# Revit family: Lighting_Wall-Mounted_Nordlux_MIB-6
name_source: partatom
category: Lighting Fixtures
revit_build: Autodesk Revit 2017 (Build: 20160225_1515(x64)
units: mm (PartAtom-declared; Revit-internal decimal feet)

## family parameters
Cut with Voids When Loaded = No
Host = Face
Light Source = Yes
OmniClass Number = 23.80.70.00
OmniClass Title = Lighting
Part Type = Normal
Room Calculation Point = No
Round Connector Dimension = Use Diameter
Shared = No

## types (2) — shared parameters
AssetType = Fixed
BIMObjectName = Lighting_Wall-Mounted_Nordlux_MIB-6
Category = Indoor lighting
Collection = MIB 6
Color Filter = 16777215
ConvergoRefNr = 0143-1909-0017-DK
Description = The MIB collection is based on classical virtues of design, with an emphasis on simplicity. The adjustable lamp head provides a sleek and Nordic design look. MIB is available in several variations, and as a collection offers a great variety of applications. An indestructible lighting collection that spreads light and joy in any modern home. Design by Bønnelycke MDD. The minimalist MIB series is steeped in Nordic elegance and boasts excellent usability. MIB 6 invites you to put the spotlight on life. The narrow lamp head emits a precise and narrow directional light.
Designer = Bonnelycke MDD
Dimming Lamp Color Temperature Shift = <None>
DurationUnit = Hours
Emit Shape Visible in Rendering = No
Emit from Circle Diameter = 50 mm  [stored 0.164042 ft]
EnergyClass = A++ - A
Finish = Primary material metal, textile cable.
HasProtectiveEarth = No
IP_Code = IP20
IfcExportAs = IfcLightFixtureType
IfcExportType = NOTDEFINED
InsulationStandardClass = Class 2 (Double isolated)
LensMaterial = Glass
LightFixtureMountingType = Surface
LightFixturePlacingType = Wall
LightSource = Not included
Manufacturer = Nordlux
ManufacturerName = Nordlux
ManufacturerURL = https://www.nordlux.com
Material = Metal
NBSDescription = General purpose luminaires
NBSReference = 90-60-50/405
Name = MIB-6
NominalCurrent = 0 A
NominalDiameter = 60 mm  [stored 0.19685 ft]
NominalFrequencyRange = 50 Hz
NominalHeight = 173 mm
NominalLength = 200 mm  [stored 0.656168 ft]
NominalRadius = 30 mm  [stored 0.0984252 ft]
NominalVoltage = 230 V
NominalVoltageCalc = 0 V
NominalWidth = 100 mm  [stored 0.328084 ft]
NumberOfPoles = 1
PhaseAngle = 0.00°
Photometric Web File = 7168 Mib 6 Væg.ies
Product data url = https://www.bimobject.com
Revision = 1
Shape = Sculptured
Size = Shade: 200x60x60 mm / Base mount 85x85x30 mm
Socket = GU10
Tilt Angle = 90.00°
TotalWattage = 8 W
URL = https://www.nordlux.com
Uniclass2 = Pr_70_70_48_85
Uniclass2015Description = Surface luminaires
Uniclass2015Reference = Pr_70_70_48_85
UsageCurrent = 0 A
Version = 1
VersionDate = 01/07/2020
WarrantyDurationUnit = Hours
zero-valued in all types: Default Elevation, ElectricalDeviceNominalPower, MaintenanceFactor, NumberOfSources

## per-type parameters (varying)
| type | ArticleNumber | Color | EANNumber | Features | LightFixtureMainMaterial | ModelReference |
| MIB 6 - black | 71689903 | Black | 5701581332782 | Black textile cable 180cm. Cable can be replaced. | Black | 71689903 |
| MIB 6 - white | 71689901 | White | 5701581332683 | White textile cable 180cm. Cable can be replaced. | White | 71689901 |

note: column(s) folded — value = type name in every type: Model

note: [stored X ft] marks values corroborated as IEEE doubles in the binary element streams (Revit-internal decimal feet)

## geometry (parser evidence)
native form markers: Sweep x5
no freeform markers — native parametric forms only
